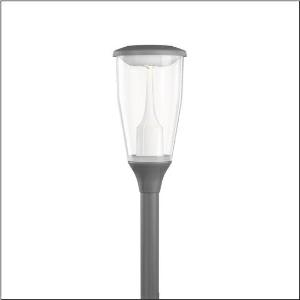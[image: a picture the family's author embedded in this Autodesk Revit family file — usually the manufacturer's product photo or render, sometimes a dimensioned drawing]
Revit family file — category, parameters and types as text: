
# Revit family: dl_11_iq___p1_0a_5xa5575bf14h000022_7e97
name_source: partatom
category: Lighting Fixtures
units: mm (PartAtom-declared; Revit-internal decimal feet)

## family parameters
Cut with Voids When Loaded = No
Host = Face
Light Source = No
Part Type = Normal
Room Calculation Point = No
Round Connector Dimension = Use Diameter
Shared = No

## types (1)
- --- (1 x LED, 1530 lm, 12.9 W, 2200K)
    Apparent Load = 13 VA
    CIE Flux Codes = 34 63 91 95 100
    Color Rendering = 70
    Color Temperature = 2200K
    Default Elevation = 1800 mm
    Description = DL 11 iQ, mast luminaire, Module 540 iQ-SR, primary light control with 3 zone facetted reflector, of plastic, silver coated, highly specular, structured, primary optical cover: cover, of PMMA, transparent, light distribution: P1.0a, light emission: direct distribution, primary light characteristic: asymmetric, installation type: post-top, LED, High Power LED, rated luminous flux: 1.560lm, luminous efficacy: 149lm/W, light colour: 722, colour temperature: 2200K, control: Street-Remote, Auto-Match, Temp-Guard, Lumen-Switch, Night-Set, Smart-Wire, Light-Fading, Desk-Remote (wireless, voltage-free reading and setting of iQ features in the workshop via application-optimized NFC function/RFID function), optimised constant luminous flux control (CLO 2.0), mains connection: 220..240V, AC, 50/60Hz, connection cable pre-assembled, cable length: 5,5m, wiring characteristics: H07RN-F, 5-core, 1.5mm², start of lifetime: 13W, end of service life: 13W, reduction: 5W, luminaire housing, upper part, of diecast aluminium, coated, Siteco® metallic grey (DB 702S), spigot size: 76mm (post-top), post-top mast mounting element, of diecast aluminium, coated, Siteco® metallic grey (DB 702S), Module 540 iQ-SR, traffic white (RAL 9016), equipment: standard, protection rating (complete): IP66, insulation class (complete): insulation class II (safety insulation), certification: CE, ENEC, ENEC+, VDE, packaging unit: 1 piece

Light Distribution: P1.0a
    Height = 665 mm
    Lamp = 1 x LED
    Lamp Light Flux = 1530 lm
    Lamp Power = 12.9 W
    Lamp count = 1
    Length = 334 mm
    Luminous efficacy = 119 lm/W
    Manufacturer = Siteco
    ModVariant = No
    Model = 5XA5575BF14H000022
    Number of Poles = 1
    OnlyDefault = Yes
    Power Factor = 1
    Product Name = DL 11 iQ | P1.0a
    Product group = mast luminaire | pylon top
    ProductGroupID = 6100
    Protection Class = Protection class II
    Protection Degree = IP 66
    RLX_Detail_Level = 1
    RLX_Emergency_Light_Flux = 0 lm
    RLX_Emergency_Type = 0
    RLX_Emergency_Type_DB = No
    RlxData = <blob elided: 104817 chars, md5=c24dc01d>
    Socket = socket
    Standby Power = 0 W
    System Light Flux = 1530 lm
    System Power = 13 W
    Type Comments = factory setting: luminous flux: 100 % | dim-lin: 254 | 516 mA
    Type Image = l_1258354.jpg
    URL = http://relux.com
    VarID = @adj_060567
    Voltage = 0 V
    Weight = 0.00 kg
    Width = 0 mm  [stored 0 ft]

note: [stored X ft] marks values corroborated as IEEE doubles in the binary element streams (Revit-internal decimal feet)

## geometry (parser evidence)
native form markers: Blend x4, Sweep x11
no freeform markers — native parametric forms only
